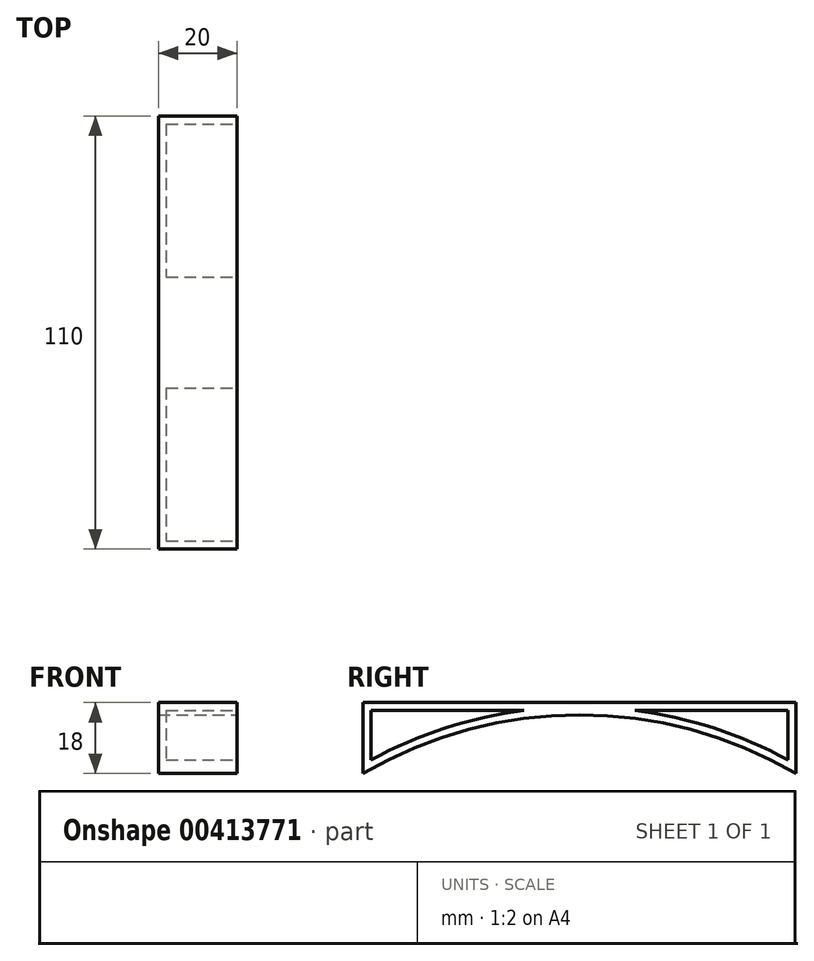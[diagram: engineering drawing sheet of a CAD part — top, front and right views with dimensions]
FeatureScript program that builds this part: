
annotation { "Feature Type Name" : "Feature", "Feature Type Description" : "" }
export const myFeature = defineFeature(function(context is Context, id is Id, definition is map)
    precondition{}
    {
        {
            var Q0;
            Q0=qCreatedBy(makeId("Top.planeOp"),FACE);
            var sketch = newSketch(context, id + "F0", { "sketchPlane" : qUnion([Q0])});
            skLineSegment(sketch, "E0.bottom", {"start": v(-10, 60) * mm, "end": v(10, 60) * mm});
            skLineSegment(sketch, "E0.top", {"start": v(-10, -50) * mm, "end": v(10, -50) * mm});
            skLineSegment(sketch, "E0.left", {"start": v(-10, 60) * mm, "end": v(-10, -50) * mm});
            skLineSegment(sketch, "E0.right", {"start": v(10, 60) * mm, "end": v(10, -50) * mm});
            skPoint(sketch, "E1", {"position": v(0, 0) * mm});
            skSolve(sketch);
        }
        {
            var Q0;
            Q0 = qSketchRegion(id + "F0", true);
            extrude(context, id + "F1", {"entities" : qUnion([Q0]), "endBound" : BoundingType.SYMMETRIC, "depth" : 18 * mm});
        }
        {
            var Q0;
            Q0=makeQuery(id+"F1.opExtrude","SWEPT_FACE",FACE,{"disambiguationData":[OSD([sQuery(id+"F0.wireOp",EDGE,"E0.right")])]});
            var sketch = newSketch(context, id + "F2", { "sketchPlane" : qUnion([Q0])});
            skCircle(sketch, "E2", {"center": v(5, -103.1) * mm, "radius": 109 * mm});
            skPoint(sketch, "E2.first.point", {"position": v(-50, -9) * mm});
            skPoint(sketch, "E2.second.point", {"position": v(60, -9) * mm});
            skPoint(sketch, "E2.third.point", {"position": v(5, 5.9) * mm});
            skSolve(sketch);
        }
        {
            var Q0;
            {var subQ1=sQuery(id+"F0.wireOp",EDGE,"E0.right");var subQ2=makeQuery(id+"F1.opExtrude","CAP_EDGE",EDGE,{"disambiguationData":[OSD([subQ1])],"isStart":true});Q0=makeQuery(id+"F2.imprint","IMPRINT",FACE,{"disambiguationData":[TD([[makeQuery(id+"F2.imprint","IMPRINT",EDGE,{"derivedFrom":subQ2}),1.0]])]});}
            var Q1;
            {var subQ1=sQuery(id+"F0.wireOp",EDGE,"E0.right");var subQ2=makeQuery(id+"F1.opExtrude","CAP_EDGE",EDGE,{"disambiguationData":[OSD([subQ1])],"isStart":true});Q1=makeQuery(id+"F2.imprint","IMPRINT",FACE,{"disambiguationData":[TD([[makeQuery(id+"F2.imprint","IMPRINT",EDGE,{"derivedFrom":subQ2}),-1.0]])]});}
            var Q2;
            Q2=sQuery(id+"F2.wireOp",EDGE,"E2");
            extrude(context, id + "F3", {"entities" : qUnion([Q0, Q1]), "operationType" : NewBodyOperationType.REMOVE, "surfaceEntities" : qUnion([Q2]), "oppositeDirection" : true, "depth" : 20 * mm});
        }
        {
            var Q0;
            Q0=makeQuery(id+"F1.opExtrude","SWEPT_FACE",FACE,{"disambiguationData":[OSD([sQuery(id+"F0.wireOp",EDGE,"E0.right")])]});
            shell(context, id + "F4", {"entities" : qUnion([Q0]), "thickness" : 2 * mm});
        }
    });
